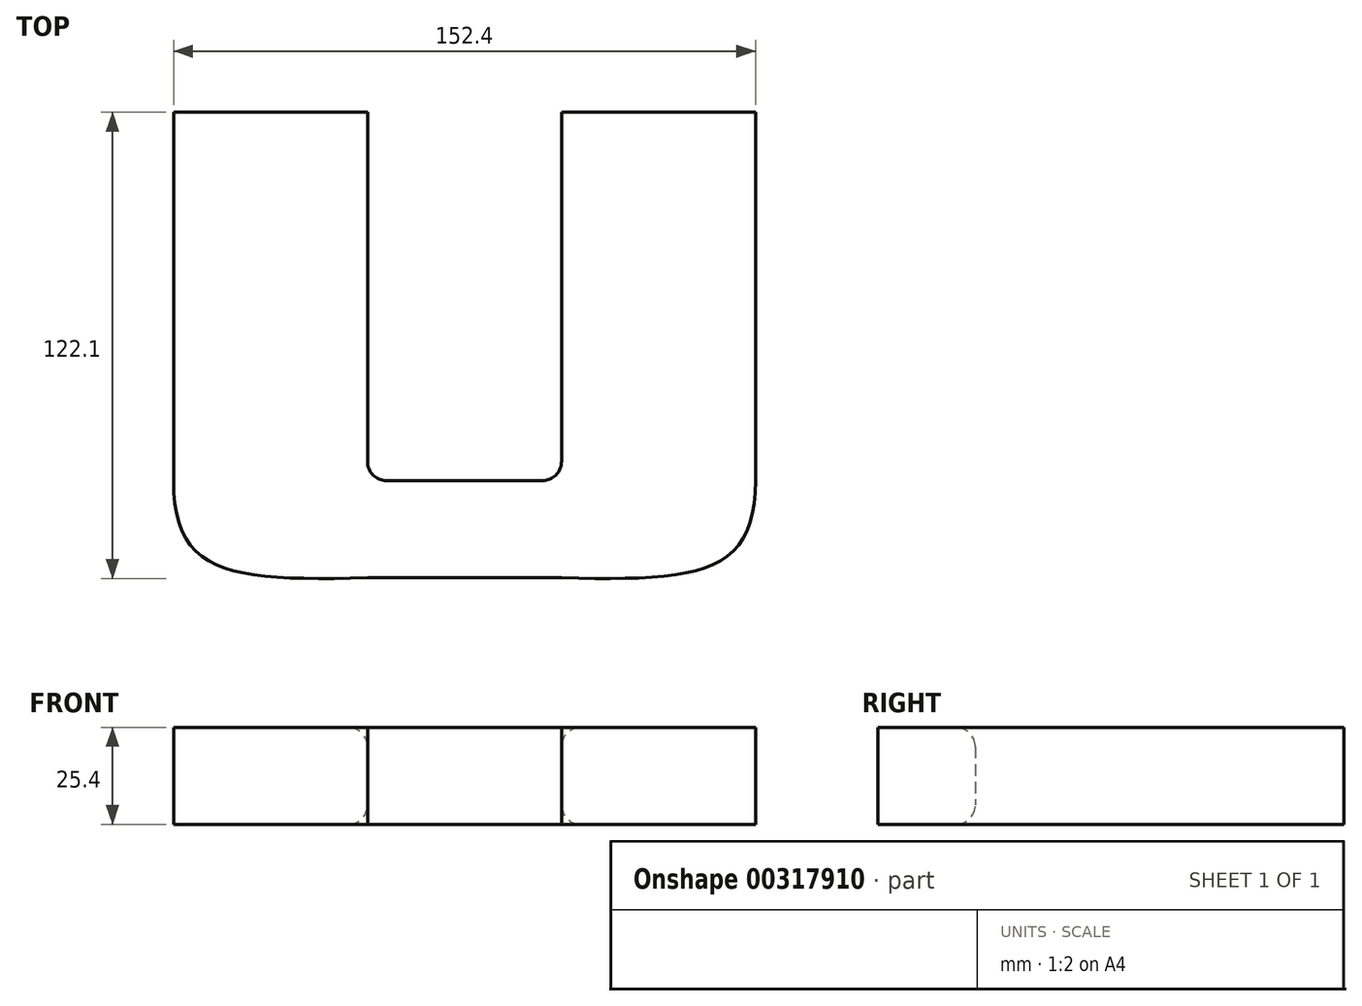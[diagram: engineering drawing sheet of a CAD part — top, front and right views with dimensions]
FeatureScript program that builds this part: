
annotation { "Feature Type Name" : "Feature", "Feature Type Description" : "" }
export const myFeature = defineFeature(function(context is Context, id is Id, definition is map)
    precondition{}
    {
        {
            var Q0;
            Q0=qCreatedBy(makeId("Top.planeOp"),FACE);
            var sketch = newSketch(context, id + "F0", { "sketchPlane" : qUnion([Q0])});
            skLineSegment(sketch, "E0.bottom", {"start": v(-25.4, 48.26) * mm, "end": v(25.4, 48.26) * mm});
            skLineSegment(sketch, "E0.top", {"start": v(-25.4, -48.26) * mm, "end": v(25.4, -48.26) * mm});
            skLineSegment(sketch, "E0.left", {"start": v(-25.4, 48.26) * mm, "end": v(-25.4, -48.26) * mm});
            skLineSegment(sketch, "E0.right", {"start": v(25.4, 48.26) * mm, "end": v(25.4, -48.26) * mm});
            skPoint(sketch, "E0.middle", {"position": v(0, 0) * mm});
            skLineSegment(sketch, "E1.bottom", {"start": v(25.4, -48.26) * mm, "end": v(50.8, -48.26) * mm});
            skLineSegment(sketch, "E1.top", {"start": v(25.4, -73.66) * mm, "end": v(50.8, -73.66) * mm});
            skLineSegment(sketch, "E1.left", {"start": v(25.4, -48.26) * mm, "end": v(25.4, -73.66) * mm});
            skLineSegment(sketch, "E1.right", {"start": v(50.8, -48.26) * mm, "end": v(50.8, -73.66) * mm});
            skFitSpline(sketch, "E2", {"points": [v(-25.4, -48.26) * mm, v(25.4, -73.66) * mm], "startDerivative": vector(0, -74.9) * mm, "endDerivative": vector(105.9, 2.58) * mm});
            skSolve(sketch);
        }
        {
            var Q0;
            Q0 = qSketchRegion(id + "F0", true);
            extrude(context, id + "F1", {"entities" : qUnion([Q0]), "depth" : 25.4 * mm});
        }
        {
            var Q0;
            Q0=makeQuery(id+"F1.opExtrude","CAP_EDGE",EDGE,{"disambiguationData":[OSD([sQuery(id+"F0.wireOp",EDGE,"E0.right")])],"isStart":false});
            var Q1;
            Q1=makeQuery(id+"F1.opExtrude","CAP_EDGE",EDGE,{"disambiguationData":[OSD([sQuery(id+"F0.wireOp",EDGE,"E1.bottom")])],"isStart":false});
            var Q2;
            Q2=makeQuery(id+"F1.opExtrude","CAP_EDGE",EDGE,{"disambiguationData":[OSD([sQuery(id+"F0.wireOp",EDGE,"E1.bottom")])],"isStart":true});
            var Q3;
            Q3=makeQuery(id+"F1.opExtrude","CAP_EDGE",EDGE,{"disambiguationData":[OSD([sQuery(id+"F0.wireOp",EDGE,"E0.right")])],"isStart":true});
            var Q4;
            Q4=makeQuery(id+"F1.opExtrude","SWEPT_EDGE",EDGE,{"disambiguationData":[OSD([sQuery(id+"F0.wireOp",EDGE,"E0.top"),sQuery(id+"F0.wireOp",EDGE,"E0.right"),sQuery(id+"F0.wireOp",EDGE,"E1.bottom"),sQuery(id+"F0.wireOp",EDGE,"E1.left")])]});
            fillet(context, id + "F2", {"entities" : qUnion([Q0, Q1, Q2, Q3, Q4]), "radius" : 5.08 * mm, "tangentPropagation" : true, "allowEdgeOverflow" : false});
        }
        {
            var Q0;
            Q0=makeQuery(id+"F1.opExtrude","SWEPT_BODY",BODY,{"disambiguationData":[OSD([sQuery(id+"F0.wireOp",EDGE,"E0.bottom"),sQuery(id+"F0.wireOp",EDGE,"E0.left"),sQuery(id+"F0.wireOp",EDGE,"E0.right"),sQuery(id+"F0.wireOp",EDGE,"E1.bottom"),sQuery(id+"F0.wireOp",EDGE,"E1.top"),sQuery(id+"F0.wireOp",EDGE,"E1.right"),sQuery(id+"F0.wireOp",EDGE,"E2")])]});
            var Q1;
            Q1=makeQuery(id+"F1.opExtrude","SWEPT_FACE",FACE,{"disambiguationData":[OSD([sQuery(id+"F0.wireOp",EDGE,"E1.right")])]});
            mirror(context, id + "F3", {"operationType" : NewBodyOperationType.ADD, "entities" : qUnion([Q0]), "mirrorPlane" : qUnion([Q1])});
        }
    });
